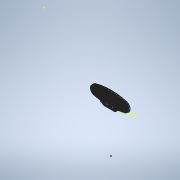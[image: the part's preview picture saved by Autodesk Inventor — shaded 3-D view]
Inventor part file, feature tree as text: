
AUTODESK INVENTOR PART (.ipt)
format: ipt  version: 2020 (Build 240168000, 168)  size: 231,936 bytes
history: native  units: mm
features: sketch x2, extrude x2, chamfer x2
ambient origin geometry x8: Origin, YZ Plane, XZ Plane, XY Plane, X Axis, Y Axis, Z Axis, Center Point
bodies: Volumenkörper1 (feature_tree), Body1 (feature_tree)
feature tree (6):
  sketch  "Skizze2"  dims[d2=11.0mm d3=0.0mm d4=0.0mm d5=10.0mm d6=0.0mm d7=1.5mm d8=2.0mm d9=45.0deg d10=1.0mm d11=2.0mm d12=45.0deg]
  sketch  "Skizze1"  dims[d0=50.0mm d1=100.0mm]
  extrude  "Extrusion1"  Depth=100.0mm
  extrude  "Extrusion2"  TaperAngle=0.0deg  [1 undecoded]
  chamfer  "Fase1"  Distance=10.0mm
  chamfer  "Fase2"  Distance=1.5mm Angle=45.0deg
note: 1 required parameter value undecoded (feature->parameter linkage not recoverable at this tier; creation-order binding heuristic only, values carry confidence <= 0.55)
